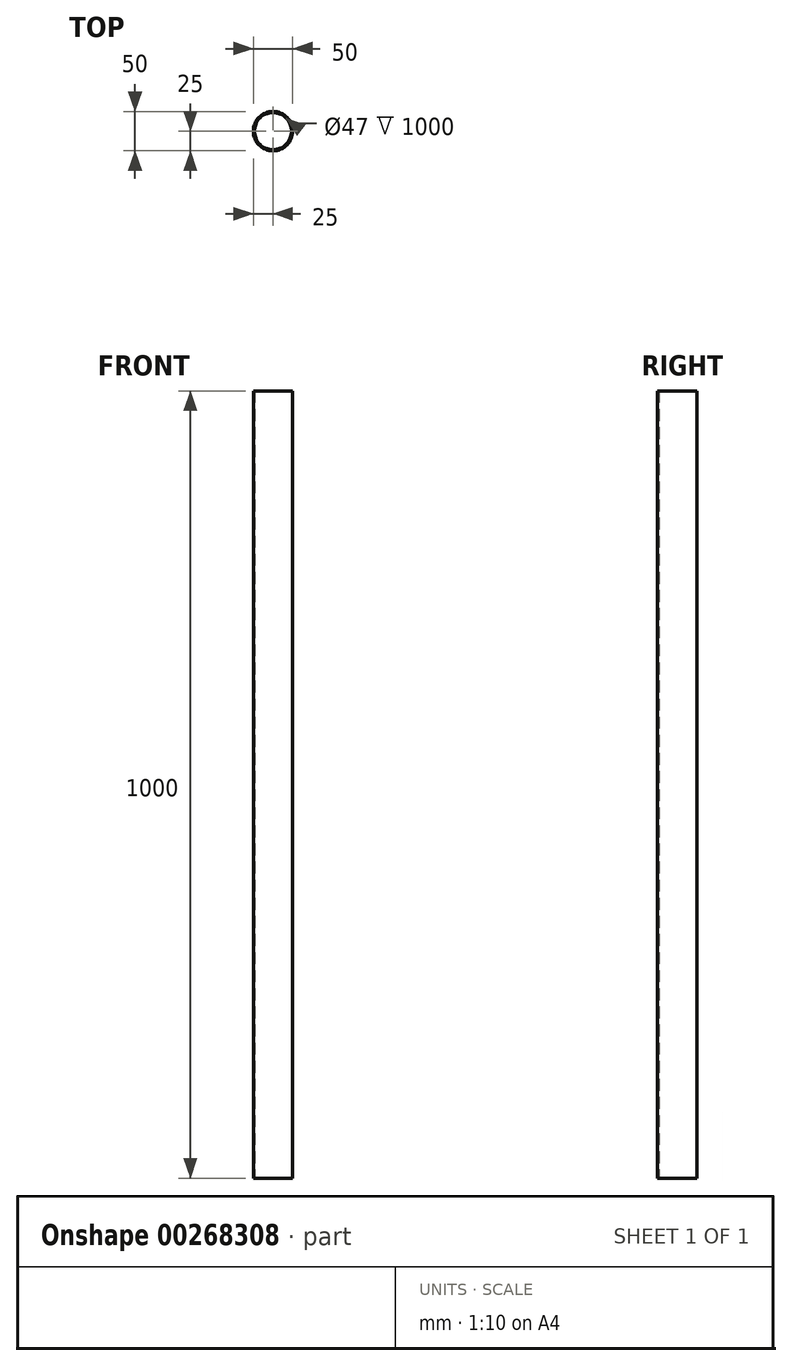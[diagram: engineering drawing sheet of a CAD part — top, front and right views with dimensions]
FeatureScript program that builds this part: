
annotation { "Feature Type Name" : "Feature", "Feature Type Description" : "" }
export const myFeature = defineFeature(function(context is Context, id is Id, definition is map)
    precondition{}
    {
        {
            var Q0;
            Q0=qCreatedBy(makeId("Top.planeOp"),FACE);
            var sketch = newSketch(context, id + "F0", { "sketchPlane" : qUnion([Q0])});
            skCircle(sketch, "E0", {"center": v(0, 0) * mm, "radius": 25 * mm});
            skCircle(sketch, "E1", {"center": v(0, 0) * mm, "radius": 23.5 * mm});
            skSolve(sketch);
        }
        {
            var Q0;
            Q0=makeQuery(id+"F0.imprint","IMPRINT",FACE,{"disambiguationData":[TD([[makeQuery(id+"F0.imprint","IMPRINT",EDGE,{"derivedFrom":sQuery(id+"F0.wireOp",EDGE,"E0")}),1.0]])]});
            extrude(context, id + "F1", {"entities" : qUnion([Q0]), "depth" : 1000 * mm});
        }
    });
